# Revit family: Вентиляторы AIRNED-M V1
name_source: partatom
category: Оборудование
revit_build: Autodesk Revit 2017 (Build: 20160225_1515(x64)
units: mm (PartAtom-declared; Revit-internal decimal feet)

## family parameters
Всегда вертикально = Да
На основе рабочей плоскости = Нет
Общий = Нет
При загрузке вырезать с полостями = Нет
Размер круглого соединителя = Использовать диаметр
Тип детали = Нормальный
Точка расчета площади = Нет

## types (14) — shared parameters
h = 130 мм
Единица измерения = шт.
Завод изготовитель = NED
Ключевая пометка = Вентиляция
Наименование и тех.хар-ка = Секция вентилятора с назад загнутыми лопатками и выбросом прямо
Раздел = ОВ
высота ножек = 120 мм

## per-type parameters (varying)
| type | А | А1 | Б | Б1 | Высота | Д | Д1 | Материал | Середина | Ширина |
| AIRNED-M 6 V1.0. | 1100 мм | 1080 мм | 1100 мм | 1080 мм | 1025 мм | 1100 мм | 1080 мм | RAL 0000 Серый металл | 670 мм | 1025 мм |
| AIRNED-M 7 V1.0. | 1100 мм | 1080 мм | 1320 мм | 1300 мм | 1245 мм | 1100 мм | 1080 мм | Сталь серая | 780 мм | 1025 мм |
| AIRNED-M 8 V1.0. | 1320 мм | 1300 мм | 1320 мм | 1300 мм | 1245 мм | 1100 мм | 1080 мм | Сталь серая | 780 мм | 1025 мм |
| AIRNED-M 8 V1.1. | 1320 мм | 1300 мм | 1320 мм | 1300 мм | 1245 мм | 1625 мм | 1605 мм | Сталь серая | 780 мм | 1550 мм |
| AIRNED-M 12 V1.0. | 1435 мм | 1415 мм | 1435 мм | 1415 мм | 1360 мм | 1100 мм | 1080 мм | Сталь серая | 838 мм | 1025 мм |
| AIRNED-M 12 V1.1. | 1435 мм | 1415 мм | 1435 мм | 1415 мм | 1360 мм | 1625 мм | 1605 мм | Сталь серая | 838 мм | 1550 мм |
| AIRNED-M 20 V1.0. | 1660 мм | 1640 мм | 1660 мм | 1640 мм | 1585 мм | 1100 мм | 1080 мм | Сталь серая | 950 мм | 1025 мм |
| AIRNED-M 20 V1.1. | 1660 мм | 1640 мм | 1660 мм | 1640 мм | 1585 мм | 1625 мм | 1605 мм | Сталь серая | 950 мм | 1550 мм |
| AIRNED-M 25 V1.1. | 2045 мм | 2025 мм | 2045 мм | 2025 мм | 1970 мм | 1625 мм | 1605 мм | Сталь серая | 1143 мм | 1550 мм |
| AIRNED-M 30 V1.1. | 2485 мм | 2465 мм | 2045 мм | 2025 мм | 1970 мм | 1625 мм | 1605 мм | Сталь серая | 1143 мм | 1550 мм |
| AIRNED-M 30 V1.2. | 2485 мм | 2465 мм | 2045 мм | 2025 мм | 1970 мм | 2150 мм | 2130 мм | Сталь серая | 1143 мм | 2075 мм |
| AIRNED-M 35 V1.2. | 2485 мм | 2465 мм | 2485 мм | 2465 мм | 2410 мм | 2150 мм | 2130 мм | Сталь серая | 1363 мм | 2075 мм |
| AIRNED-M 40 V1.1. | 3320 мм | 3300 мм | 3320 мм | 3300 мм | 3245 мм | 1625 мм | 1605 мм | Сталь серая | 1780 мм | 1550 мм |
| AIRNED-M 45 V1.1. | 3320 мм | 3300 мм | 4090 мм | 4070 мм | 4015 мм | 1625 мм | 1605 мм | Сталь серая | 2165 мм | 1550 мм |

note: column(s) folded — value = type name in every type: Тип, марка, обозначение
